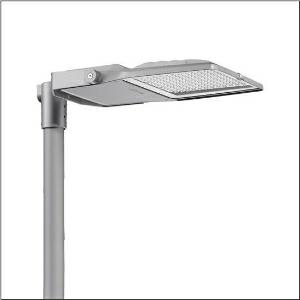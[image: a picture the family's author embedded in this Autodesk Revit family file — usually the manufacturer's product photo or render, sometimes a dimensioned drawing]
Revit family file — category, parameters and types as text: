
# Revit family: floodlight_fl_21_iq_midi___pl64_5xa7781e2e3a_93f0
name_source: partatom
category: Lighting Fixtures
units: mm (PartAtom-declared; Revit-internal decimal feet)

## family parameters
Cut with Voids When Loaded = No
Host = Face
Light Source = No
Part Type = Normal
Room Calculation Point = No
Round Connector Dimension = Use Diameter
Shared = No

## types (1)
- --- (1 x LED, 25930 lm, 208.1 W, 3000K)
    Apparent Load = 208 VA
    CIE Flux Codes = 28 80 98 100 100
    Color Rendering = 70
    Color Temperature = 3000K
    Default Elevation = 1800 mm
    Description = Floodlight FL 21 iQ midi, floodlight, primary light control with lens, of PMMA, primary optical cover: protective disc, of toughened safety glass, transparent, light distribution: PL64, light emission: direct distribution, installation type: surface-mounted, lamps: LED, High Power LED, rated values: 25.930lm | 208,1W | 124,6lm/W (begin service life); end service life: 25.930lm | 227,1W; at 50% lumin. flux: 12.965lm | 90,1W | 143,9lm/W, colour temperature: 3000K, colour rendering: CRI > 70, light colour: 730, light setting 1 begin service life: 100% | 25.930lm | 208,1W | 124,6lm/W | 3.000K, light setting 1 end service life: 227,1W, further light settings possible, control: optimised constant luminous flux control (CLO 2.0), Desk-Remote (wireless, voltage-free reading and setting of iQ features in the workshop via application-optimized NFC function/RFID function), Light-Fading, Smart-Wire, Night-Set, Lumen-Switch, Temp-Guard, Auto-Match, pre-setting: linear dimming characteristic, with terminal, 6-pole, mains connection: 220..240V, AC, 50/60Hz, luminaire housing, of diecast aluminium, powder-coated, SITECO metallic grey (DB 702S), corrosivity category C5 mid according to DIN EN ISO 12944suitable for swimming poolschlorine-resistant, sealing non-destructively replaceable, please order mast flange separately, mast bracket, of steel, galvanised, powder-coated, SITECO metallic grey (DB 702S), protection rating (complete): IP66, insulation class (complete): insulation class II (safety insulation), certification: CE, ENEC, VDE, protection symbol: D, impact resistance: IK08, permissible operating ambient temperature: -40..+40°C, permissible operating ambient temperature for outdoor applications: -40..+50°C, standard: DIN EN 12944, LABS conformity tested according to VDMA 24364:2018-05, packaging unit: 1 piece

Light Distribution: PL64
    Height = 76 mm
    Lamp = 1 x LED
    Lamp Light Flux = 25930 lm
    Lamp Power = 208.1 W
    Lamp count = 1
    Length = 657 mm
    Luminous efficacy = 125 lm/W
    Manufacturer = Siteco
    ModVariant = No
    Model = 5XA7781E2E3A
    Number of Poles = 1
    OnlyDefault = Yes
    Power Factor = 1
    Product Name = Floodlight FL 21 iQ midi | PL64
    Product group = floodlight | pylon annexe
    ProductGroupID = 6201
    Protection Class = Protection class II
    Protection Degree = IP 66
    RLX_Detail_Level = 1
    RLX_Emergency_Light_Flux = 0 lm
    RLX_Emergency_Type = 0
    RLX_Emergency_Type_DB = No
    RlxData = <blob elided: 153901 chars, md5=6ab7bf4f>
    Socket = socket
    Standby Power = 0 W
    System Light Flux = 25930 lm
    System Power = 208 W
    Type Comments = factory setting: luminous flux: 100 % | dim-lin: 254 | 710 mA
    Type Image = l_1007123.jpg
    URL = http://relux.com
    VarID = @adj_107231
    Voltage = 0 V
    Weight = 0.00 kg
    Width = 442 mm

## geometry (parser evidence)
native form markers: Blend x4, Sweep x11
no freeform markers — native parametric forms only
